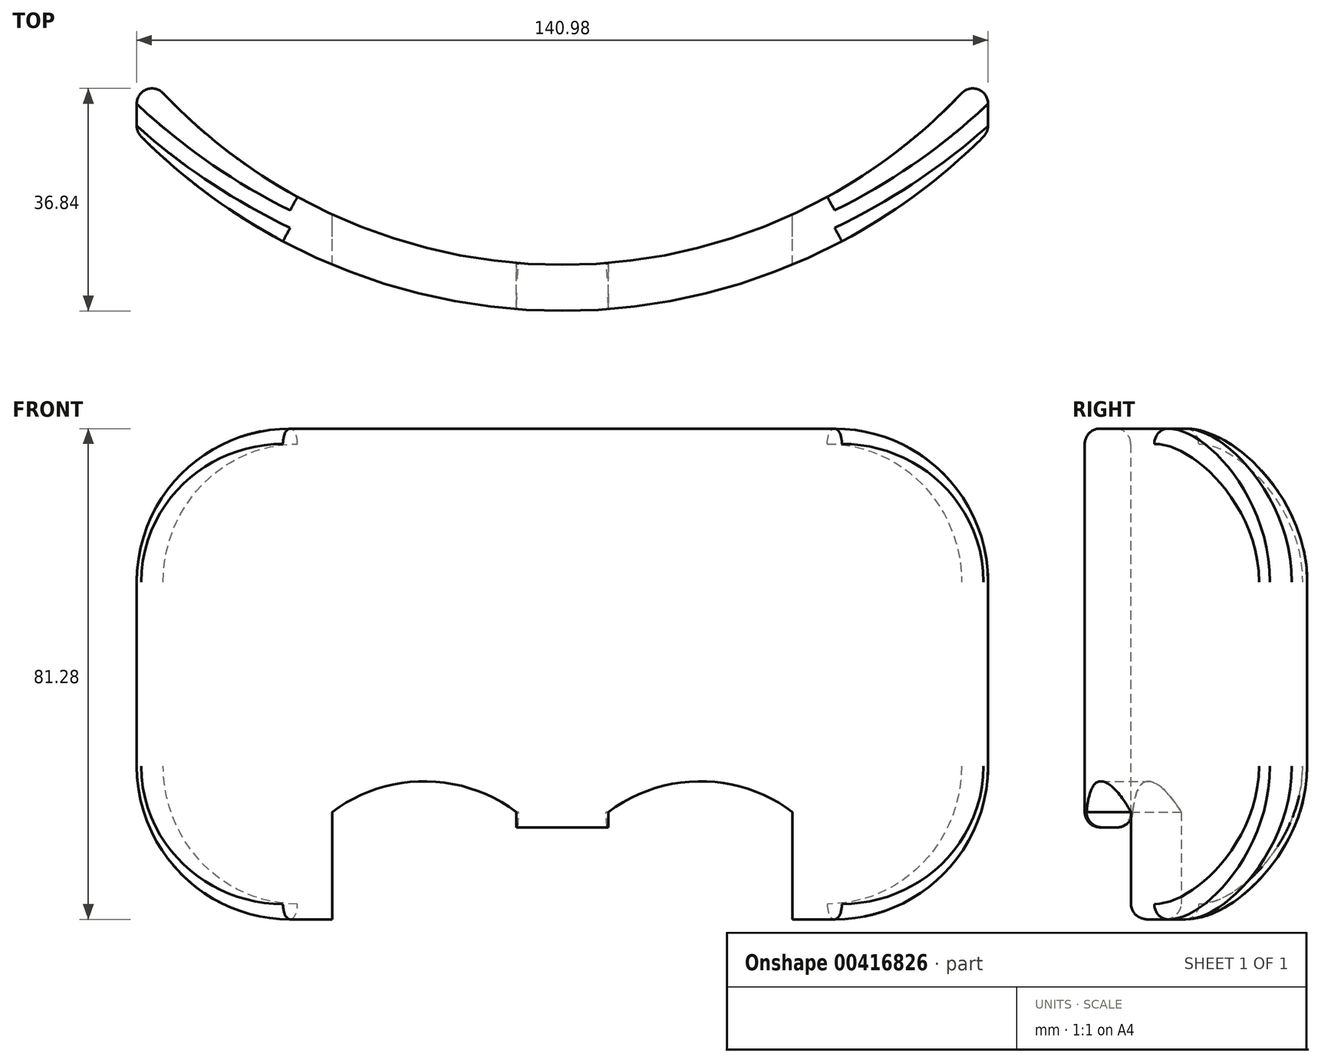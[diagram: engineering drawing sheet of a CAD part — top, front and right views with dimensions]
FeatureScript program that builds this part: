
annotation { "Feature Type Name" : "Feature", "Feature Type Description" : "" }
export const myFeature = defineFeature(function(context is Context, id is Id, definition is map)
    precondition{}
    {
        {
            var Q0;
            Q0=qCreatedBy(makeId("Top.planeOp"),FACE);
            var sketch = newSketch(context, id + "F0", { "sketchPlane" : qUnion([Q0])});
            skArc(sketch, "E0", {"start": v(-70.48, -11.41) * mm, "mid": v(0, -41.03) * mm, "end": v(70.49, -11.41) * mm});
            skLineSegment(sketch, "E1", {"start": v(0, 0) * mm, "end": v(0, 211.05) * mm, "construction": true});
            skArc(sketch, "E2", {"start": v(-70.48, 0) * mm, "mid": v(0, -33.4) * mm, "end": v(70.48, 0) * mm});
            skLineSegment(sketch, "E3", {"start": v(-70.49, 0) * mm, "end": v(-70.49, -11.41) * mm});
            skLineSegment(sketch, "E4", {"start": v(70.48, 0) * mm, "end": v(70.48, -11.41) * mm});
            skLineSegment(sketch, "E5", {"start": v(70.48, 0) * mm, "end": v(-70.48, 0) * mm, "construction": true});
            skSolve(sketch);
        }
        {
            var Q0;
            Q0=makeQuery(id+"F0.imprint","IMPRINT",FACE,{"disambiguationData":[TD([[makeQuery(id+"F0.imprint","IMPRINT",EDGE,{"derivedFrom":sQuery(id+"F0.wireOp",EDGE,"E0")}),1.0]])]});
            extrude(context, id + "F1", {"entities" : qUnion([Q0]), "depth" : 81.28 * mm, "offsetDistance" : 25.4 * mm});
        }
        {
            var Q0;
            Q0=qCreatedBy(makeId("Front.planeOp"),FACE);
            var sketch = newSketch(context, id + "F2", { "sketchPlane" : qUnion([Q0])});
            skLineSegment(sketch, "E6.bottom", {"start": v(-50.8, 73.66) * mm, "end": v(50.8, 73.66) * mm});
            skLineSegment(sketch, "E6.left", {"start": v(-63.5, 60.96) * mm, "end": v(-63.5, 21.59) * mm});
            skLineSegment(sketch, "E6.right", {"start": v(63.5, 60.96) * mm, "end": v(63.5, 21.6) * mm});
            skPoint(sketch, "E7.visualSharp", {"position": v(-63.5, 73.66) * mm});
            skArc(sketch, "E7.filletArc", {"start": v(-50.8, 73.66) * mm, "mid": v(-59.78, 69.94) * mm, "end": v(-63.5, 60.96) * mm});
            skPoint(sketch, "E8.visualSharp", {"position": v(63.5, 73.66) * mm});
            skArc(sketch, "E8.filletArc", {"start": v(63.5, 60.96) * mm, "mid": v(59.78, 69.94) * mm, "end": v(50.8, 73.66) * mm});
            skLineSegment(sketch, "E9", {"start": v(57.15, 15.24) * mm, "end": v(19.1, 15.24) * mm});
            skLineSegment(sketch, "E10", {"start": v(-19.1, 15.24) * mm, "end": v(-57.15, 15.24) * mm});
            skLineSegment(sketch, "E11", {"start": v(0, 0) * mm, "end": v(0, 74.9) * mm, "construction": true});
            skLineSegment(sketch, "E12", {"start": v(-16.71, 16.91) * mm, "end": v(-15.74, 19.58) * mm});
            skLineSegment(sketch, "E13", {"start": v(-3.8, 27.94) * mm, "end": v(3.8, 27.94) * mm});
            skLineSegment(sketch, "E14", {"start": v(15.74, 19.58) * mm, "end": v(16.71, 16.91) * mm});
            skPoint(sketch, "E15.visualSharp", {"position": v(-12.7, 27.94) * mm});
            skArc(sketch, "E15.filletArc", {"start": v(-3.8, 27.94) * mm, "mid": v(-11.1, 25.64) * mm, "end": v(-15.74, 19.58) * mm});
            skPoint(sketch, "E16.visualSharp", {"position": v(12.7, 27.94) * mm});
            skArc(sketch, "E16.filletArc", {"start": v(15.74, 19.58) * mm, "mid": v(11.1, 25.64) * mm, "end": v(3.8, 27.94) * mm});
            skPoint(sketch, "E17.visualSharp", {"position": v(-17.32, 15.24) * mm});
            skArc(sketch, "E17.filletArc", {"start": v(-19.1, 15.24) * mm, "mid": v(-17.64, 15.7) * mm, "end": v(-16.71, 16.91) * mm});
            skPoint(sketch, "E18.visualSharp", {"position": v(17.32, 15.24) * mm});
            skArc(sketch, "E18.filletArc", {"start": v(16.71, 16.91) * mm, "mid": v(17.64, 15.7) * mm, "end": v(19.1, 15.24) * mm});
            skPoint(sketch, "E19.visualSharp", {"position": v(-63.5, 15.24) * mm});
            skArc(sketch, "E19.filletArc", {"start": v(-63.5, 21.59) * mm, "mid": v(-61.64, 17.1) * mm, "end": v(-57.15, 15.24) * mm});
            skPoint(sketch, "E20.visualSharp", {"position": v(63.5, 15.24) * mm});
            skArc(sketch, "E20.filletArc", {"start": v(57.15, 15.24) * mm, "mid": v(61.64, 17.1) * mm, "end": v(63.5, 21.6) * mm});
            skLineSegment(sketch, "E21", {"start": v(19.1, 15.24) * mm, "end": v(-19.1, 15.24) * mm});
            skLineSegment(sketch, "E22", {"start": v(88.9, 0) * mm, "end": v(88.9, 83.82) * mm});
            skLineSegment(sketch, "E23", {"start": v(-88.9, 83.82) * mm, "end": v(-88.9, 0) * mm});
            skLineSegment(sketch, "E24", {"start": v(-88.9, 0) * mm, "end": v(88.9, 0) * mm});
            skLineSegment(sketch, "E25", {"start": v(88.9, 83.82) * mm, "end": v(-88.9, 83.82) * mm});
            skSolve(sketch);
        }
        {
            var Q0;
            Q0=qCreatedBy(makeId("Top.planeOp"),FACE);
            var sketch = newSketch(context, id + "F3", { "sketchPlane" : qUnion([Q0])});
            skCircle(sketch, "E26", {"center": v(0, 57.15) * mm, "radius": 98.68 * mm});
            skCircle(sketch, "E27", {"center": v(0, 57.15) * mm, "radius": 97.4 * mm});
            skLineSegment(sketch, "E28", {"start": v(-89.52, 0) * mm, "end": v(0, 0) * mm, "construction": true});
            skLineSegment(sketch, "E29", {"start": v(-71.12, 0) * mm, "end": v(-71.12, -9.41) * mm});
            skLineSegment(sketch, "E30", {"start": v(-63.5, 0) * mm, "end": v(-63.5, -16.72) * mm});
            skLineSegment(sketch, "E31.MirrorCS", {"start": v(71.12, 0) * mm, "end": v(71.12, -9.41) * mm});
            skLineSegment(sketch, "E32.MirrorCS", {"start": v(89.52, 0) * mm, "end": v(0, 0) * mm, "construction": true});
            skLineSegment(sketch, "E33.MirrorCS", {"start": v(63.5, 0) * mm, "end": v(63.5, -16.72) * mm});
            skLineSegment(sketch, "E34", {"start": v(-71.12, 0) * mm, "end": v(-63.5, 0) * mm});
            skLineSegment(sketch, "E35", {"start": v(63.5, 0) * mm, "end": v(71.12, 0) * mm});
            skSolve(sketch);
        }
        {
            var Q0;
            Q0=makeQuery(id+"F1.opExtrude","CAP_EDGE",EDGE,{"disambiguationData":[OSD([sQuery(id+"F0.wireOp",EDGE,"E3")])],"isStart":false});
            var Q1;
            Q1=makeQuery(id+"F1.opExtrude","CAP_EDGE",EDGE,{"disambiguationData":[OSD([sQuery(id+"F0.wireOp",EDGE,"E4")])],"isStart":false});
            var Q2;
            Q2=makeQuery(id+"F1.opExtrude","CAP_EDGE",EDGE,{"disambiguationData":[OSD([sQuery(id+"F0.wireOp",EDGE,"E3")])],"isStart":true});
            var Q3;
            Q3=makeQuery(id+"F1.opExtrude","CAP_EDGE",EDGE,{"disambiguationData":[OSD([sQuery(id+"F0.wireOp",EDGE,"E4")])],"isStart":true});
            fillet(context, id + "F4", {"entities" : qUnion([Q0, Q1, Q2, Q3]), "radius" : 25.4 * mm, "tangentPropagation" : true, "allowEdgeOverflow" : false});
        }
        {
            var Q0;
            Q0=makeQuery(id+"F2.imprint","IMPRINT",FACE,{"disambiguationData":[TD([[makeQuery(id+"F2.imprint","IMPRINT",EDGE,{"derivedFrom":sQuery(id+"F2.wireOp",EDGE,"E6.bottom")}),1.0]])]});
            var sketch = newSketch(context, id + "F5", { "sketchPlane" : qUnion([Q0])});
            skLineSegment(sketch, "E36", {"start": v(-12.7, 0) * mm, "end": v(-9.53, 15.24) * mm});
            skLineSegment(sketch, "E37", {"start": v(-9.53, 15.24) * mm, "end": v(9.52, 15.24) * mm});
            skLineSegment(sketch, "E38", {"start": v(9.52, 15.24) * mm, "end": v(12.7, 0) * mm});
            skLineSegment(sketch, "E39", {"start": v(12.7, 0) * mm, "end": v(-12.7, 0) * mm});
            skSolve(sketch);
        }
        {
            var Q0;
            Q0=qSketchRegion(id+"F5",true);
            extrude(context, id + "F6", {"entities" : qUnion([Q0]), "operationType" : NewBodyOperationType.REMOVE, "endBound" : BoundingType.THROUGH_ALL, "depth" : 25.4 * mm, "offsetDistance" : 25.4 * mm});
        }
        {
            var Q0;
            Q0=makeQuery(id+"F6.boolean.opBoolean","COPY",EDGE,{"derivedFrom":makeQuery(id+"F6.opExtrude","SWEPT_EDGE",EDGE,{"disambiguationData":[OSD([sQuery(id+"F2.wireOp",EDGE,"E21"),sQuery(id+"F5.wireOp",EDGE,"E36"),sQuery(id+"F5.wireOp",EDGE,"E37")])]})});
            var Q1;
            Q1=makeQuery(id+"F6.boolean.opBoolean","COPY",EDGE,{"derivedFrom":makeQuery(id+"F6.opExtrude","SWEPT_EDGE",EDGE,{"disambiguationData":[OSD([sQuery(id+"F2.wireOp",EDGE,"E21"),sQuery(id+"F5.wireOp",EDGE,"E37"),sQuery(id+"F5.wireOp",EDGE,"E38")])]})});
            var Q2;
            Q2=makeQuery(id+"F6.boolean.opBoolean","COPY",EDGE,{"derivedFrom":makeQuery(id+"F6.opExtrude","SWEPT_EDGE",EDGE,{"disambiguationData":[OSD([sQuery(id+"F2.wireOp",EDGE,"E24"),sQuery(id+"F5.wireOp",EDGE,"E38"),sQuery(id+"F5.wireOp",EDGE,"E39")])]})});
            var Q3;
            Q3=makeQuery(id+"F6.boolean.opBoolean","COPY",EDGE,{"derivedFrom":makeQuery(id+"F6.opExtrude","SWEPT_EDGE",EDGE,{"disambiguationData":[OSD([sQuery(id+"F2.wireOp",EDGE,"E24"),sQuery(id+"F5.wireOp",EDGE,"E36"),sQuery(id+"F5.wireOp",EDGE,"E39")])]})});
            fillet(context, id + "F7", {"entities" : qUnion([Q0, Q1, Q2, Q3]), "radius" : 2.54 * mm, "tangentPropagation" : true, "allowEdgeOverflow" : false});
        }
        {
            var Q0;
            Q0=makeQuery(id+"F4.opFillet","BLEND_EDGE",EDGE,{"blendedFrom":[makeQuery(id+"F1.opExtrude","CAP_EDGE",EDGE,{"disambiguationData":[OSD([sQuery(id+"F0.wireOp",EDGE,"E4")])],"isStart":false}),makeQuery(id+"F1.opExtrude","SWEPT_FACE",FACE,{"disambiguationData":[OSD([sQuery(id+"F0.wireOp",EDGE,"E0")])]})],"blendedInto":[makeQuery(id+"F1.opExtrude","SWEPT_FACE",FACE,{"disambiguationData":[OSD([sQuery(id+"F0.wireOp",EDGE,"E0")])]})]});
            var Q1;
            Q1=makeQuery(id+"F1.opExtrude","CAP_EDGE",EDGE,{"disambiguationData":[OSD([sQuery(id+"F0.wireOp",EDGE,"E2")])],"isStart":false});
            fillet(context, id + "F8", {"entities" : qUnion([Q0, Q1]), "radius" : 2.54 * mm, "tangentPropagation" : true, "defaultsChanged" : false, "vertexSettings" : [], "allowEdgeOverflow" : false});
        }
        {
            var Q0;
            Q0=qCreatedBy(makeId("Front.planeOp"),FACE);
            var sketch = newSketch(context, id + "F9", { "sketchPlane" : qUnion([Q0])});
            skLineSegment(sketch, "E40.bottom", {"start": v(-45.72, 30.48) * mm, "end": v(45.72, 30.48) * mm});
            skLineSegment(sketch, "E40.top", {"start": v(-8.38, 17.78) * mm, "end": v(8.38, 17.78) * mm});
            skLineSegment(sketch, "E40.left", {"start": v(-50.8, 25.4) * mm, "end": v(-50.8, 17.78) * mm});
            skLineSegment(sketch, "E40.right", {"start": v(50.8, 25.4) * mm, "end": v(50.8, 17.78) * mm});
            skLineSegment(sketch, "E41", {"start": v(0, 0) * mm, "end": v(0, 124.67) * mm, "construction": true});
            skLineSegment(sketch, "E42", {"start": v(-14.54, 12.97) * mm, "end": v(-16.5, 5.08) * mm});
            skLineSegment(sketch, "E43", {"start": v(-16.5, 5.08) * mm, "end": v(-45.72, 5.08) * mm});
            skLineSegment(sketch, "E44", {"start": v(-50.8, 10.16) * mm, "end": v(-50.8, 17.78) * mm});
            skPoint(sketch, "E45.newPointB", {"position": v(-50.8, 17.78) * mm});
            skArc(sketch, "E45.filletArc", {"start": v(-8.38, 17.78) * mm, "mid": v(-12.3, 16.43) * mm, "end": v(-14.54, 12.97) * mm});
            skLineSegment(sketch, "E46.MirrorCS", {"start": v(16.5, 5.08) * mm, "end": v(45.72, 5.08) * mm});
            skLineSegment(sketch, "E47.MirrorCS", {"start": v(14.54, 12.97) * mm, "end": v(16.5, 5.08) * mm});
            skArc(sketch, "E48.MirrorCS", {"start": v(8.38, 17.78) * mm, "mid": v(12.3, 16.43) * mm, "end": v(14.54, 12.97) * mm});
            skLineSegment(sketch, "E49.MirrorCS", {"start": v(50.8, 10.16) * mm, "end": v(50.8, 17.78) * mm});
            skPoint(sketch, "E50.visualSharp", {"position": v(-50.8, 30.48) * mm});
            skArc(sketch, "E50.filletArc", {"start": v(-45.72, 30.48) * mm, "mid": v(-49.31, 29) * mm, "end": v(-50.8, 25.4) * mm});
            skPoint(sketch, "E51.visualSharp", {"position": v(50.8, 30.48) * mm});
            skArc(sketch, "E51.filletArc", {"start": v(50.8, 25.4) * mm, "mid": v(49.31, 29) * mm, "end": v(45.72, 30.48) * mm});
            skPoint(sketch, "E52.visualSharp", {"position": v(50.8, 5.08) * mm});
            skArc(sketch, "E52.filletArc", {"start": v(45.72, 5.08) * mm, "mid": v(49.31, 6.57) * mm, "end": v(50.8, 10.16) * mm});
            skPoint(sketch, "E53.visualSharp", {"position": v(-50.8, 5.08) * mm});
            skArc(sketch, "E53.filletArc", {"start": v(-50.8, 10.16) * mm, "mid": v(-49.31, 6.57) * mm, "end": v(-45.72, 5.08) * mm});
            skSolve(sketch);
        }
        {
            var Q0;
            Q0=qCreatedBy(makeId("Front.planeOp"),FACE);
            var sketch = newSketch(context, id + "F10", { "sketchPlane" : qUnion([Q0])});
            skLineSegment(sketch, "E54.bottom", {"start": v(-38.1, 0) * mm, "end": v(38.1, 0) * mm});
            skLineSegment(sketch, "E54.top", {"start": v(-7.62, 17.78) * mm, "end": v(7.62, 17.78) * mm});
            skLineSegment(sketch, "E54.left", {"start": v(-38.1, 0) * mm, "end": v(-38.1, 17.78) * mm});
            skLineSegment(sketch, "E54.right", {"start": v(38.1, 0) * mm, "end": v(38.1, 17.78) * mm});
            skArc(sketch, "E55", {"start": v(-7.62, 17.78) * mm, "mid": v(-22.86, 22.86) * mm, "end": v(-38.1, 17.78) * mm});
            skArc(sketch, "E56", {"start": v(38.1, 17.78) * mm, "mid": v(22.86, 22.86) * mm, "end": v(7.62, 17.78) * mm});
            skLineSegment(sketch, "E57", {"start": v(-7.62, 17.78) * mm, "end": v(-7.62, 0) * mm});
            skLineSegment(sketch, "E58", {"start": v(7.62, 17.78) * mm, "end": v(7.62, 0) * mm});
            skLineSegment(sketch, "E59", {"start": v(-38.1, 0) * mm, "end": v(-76.2, 0) * mm});
            skLineSegment(sketch, "E60", {"start": v(-76.2, 0) * mm, "end": v(-76.2, 88.9) * mm});
            skLineSegment(sketch, "E61", {"start": v(-76.2, 88.9) * mm, "end": v(76.2, 88.9) * mm});
            skLineSegment(sketch, "E62", {"start": v(76.2, 88.9) * mm, "end": v(76.2, 0) * mm});
            skLineSegment(sketch, "E63", {"start": v(76.2, 0) * mm, "end": v(38.1, 0) * mm});
            skSolve(sketch);
        }
        {
            var Q0;
            {var subQ0=sQuery(id+"F10.wireOp",EDGE,"E54.left");Q0=makeQuery(id+"F10.imprint","IMPRINT",FACE,{"disambiguationData":[TD([[makeQuery(id+"F10.imprint","IMPRINT",EDGE,{"derivedFrom":subQ0}),-1.0]])]});}
            var Q1;
            {var subQ2=sQuery(id+"F10.wireOp",EDGE,"E54.right");Q1=makeQuery(id+"F10.imprint","IMPRINT",FACE,{"disambiguationData":[TD([[makeQuery(id+"F10.imprint","IMPRINT",EDGE,{"derivedFrom":subQ2}),1.0]])]});}
            extrude(context, id + "F11", {"entities" : qUnion([Q0, Q1]), "operationType" : NewBodyOperationType.REMOVE, "endBound" : BoundingType.THROUGH_ALL, "depth" : 25.4 * mm, "offsetDistance" : 25.4 * mm});
        }
    });
